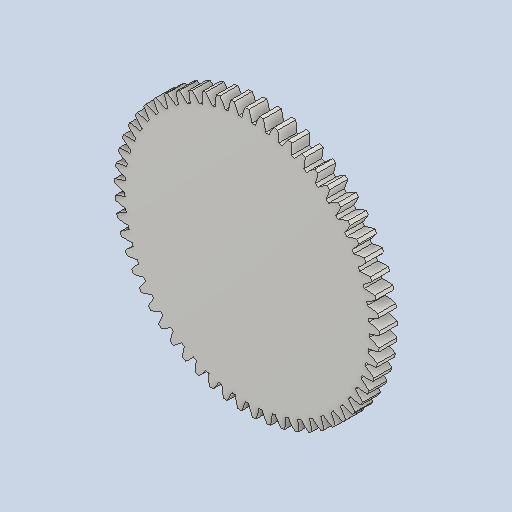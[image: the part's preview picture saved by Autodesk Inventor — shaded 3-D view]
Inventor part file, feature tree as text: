
AUTODESK INVENTOR PART (.ipt)
format: ipt  version: 2022.2 (Build 262287010, 287A)  size: 381,952 bytes
history: native  units: mm (DEFAULTED — no unit token found)
features: plane x3, other x3, sketch x2, extrude x1
ambient origin geometry x8: Origin, YZ Plane, XZ Plane, XY Plane, X Axis, Y Axis, Z Axis, Center Point
bodies: Solid1 (feature_tree)
feature tree (9):
  extrude  "Extrusion1"  Depth=8.0mm TaperAngle=0.0deg
  plane  "Work Plane2"
  plane  "Work Plane8"
  plane  "Work Plane9"
  other  "Spur Gear"
  sketch  "Sketch1"  dims[d0=118.0mm d1=8.0mm d2=0.0mm]
  sketch  "Sketch2"  dims[d3=114.0mm d4=10.0mm d5=0.0mm d16=65.0mm d17=0.0mm d34=0.551157mm d39=0.0mm d41=0.0mm d43=65.0mm d46=65.0mm d47=0.0mm d48=0.0mm]
  other  "Srf1"
  other  "Pitch Diameter"
